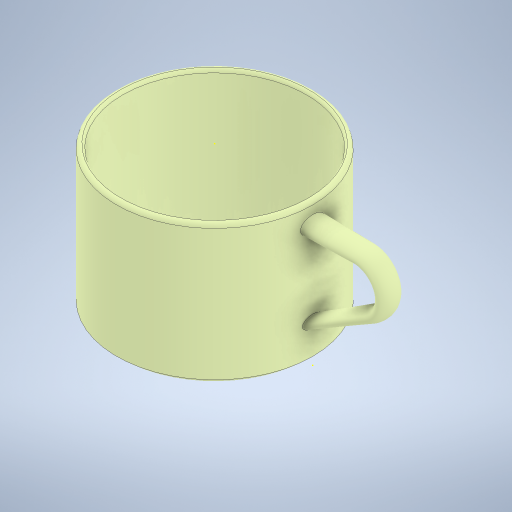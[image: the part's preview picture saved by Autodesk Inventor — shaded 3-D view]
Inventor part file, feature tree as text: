
AUTODESK INVENTOR PART (.ipt)
format: ipt  version: 2023 (Build 270158000, 158)  size: 377,344 bytes
history: native  units: in
note: dims shown in document units (in); Inventor stores cm internally (conversion verified against a paired STEP export)
features: sketch x9, plane x2, other x1, revolve x1, shell x1, loft x1, fillet x1, extrude x1
ambient origin geometry x8: Origin, YZ Plane, XZ Plane, XY Plane, X Axis, Y Axis, Z Axis, Center Point
bodies: Solid1 (feature_tree)
feature tree (17):
  other  "CrossSection1"
  sketch  "Sketch1"  dims[d0=1.2795in d1=2.7559in d2=1.7717in]
  sketch  "Sketch2"  dims[d3=2.5591in d4=90.0deg d5=0.1181in]
  revolve  "Revolution1"  [1 undecoded]
  shell  "Shell1"  Thickness=1.7717in
  sketch  "Sketch3"  dims[d6=0.0197in d7=0.0787in d8=0.0in d9=0.7874in d10=0.3937in]
  sketch  "Sketch4"  dims[d11=0.9843in]
  sketch  "Sketch5"  dims[d12=0.4724in]
  plane  "Work Plane1"
  sketch  "Sketch6"  dims[d13=0.5906in]
  plane  "Work Plane2"
  sketch  "Sketch7"  dims[d14=0.1575in]
  sketch  "Sketch8"  dims[d15=0.2362in]
  loft  "Loft1"
  fillet  "Fillet1"  Radius=0.1181in
  extrude  "Extrusion1"  Depth=0.3937in
  sketch  "Sketch9"  dims[d16=0.1181in d17=0.1969in d18=0.0in d19=90.0deg d20=0.0in d21=90.0deg d22=0.0in d23=90.0deg d24=0.0787in d25=2.5591in d26=2.4409in d27=0.0787in d28=0.0in]
note: 1 required parameter value undecoded (feature->parameter linkage not recoverable at this tier; creation-order binding heuristic only, values carry confidence <= 0.55)
